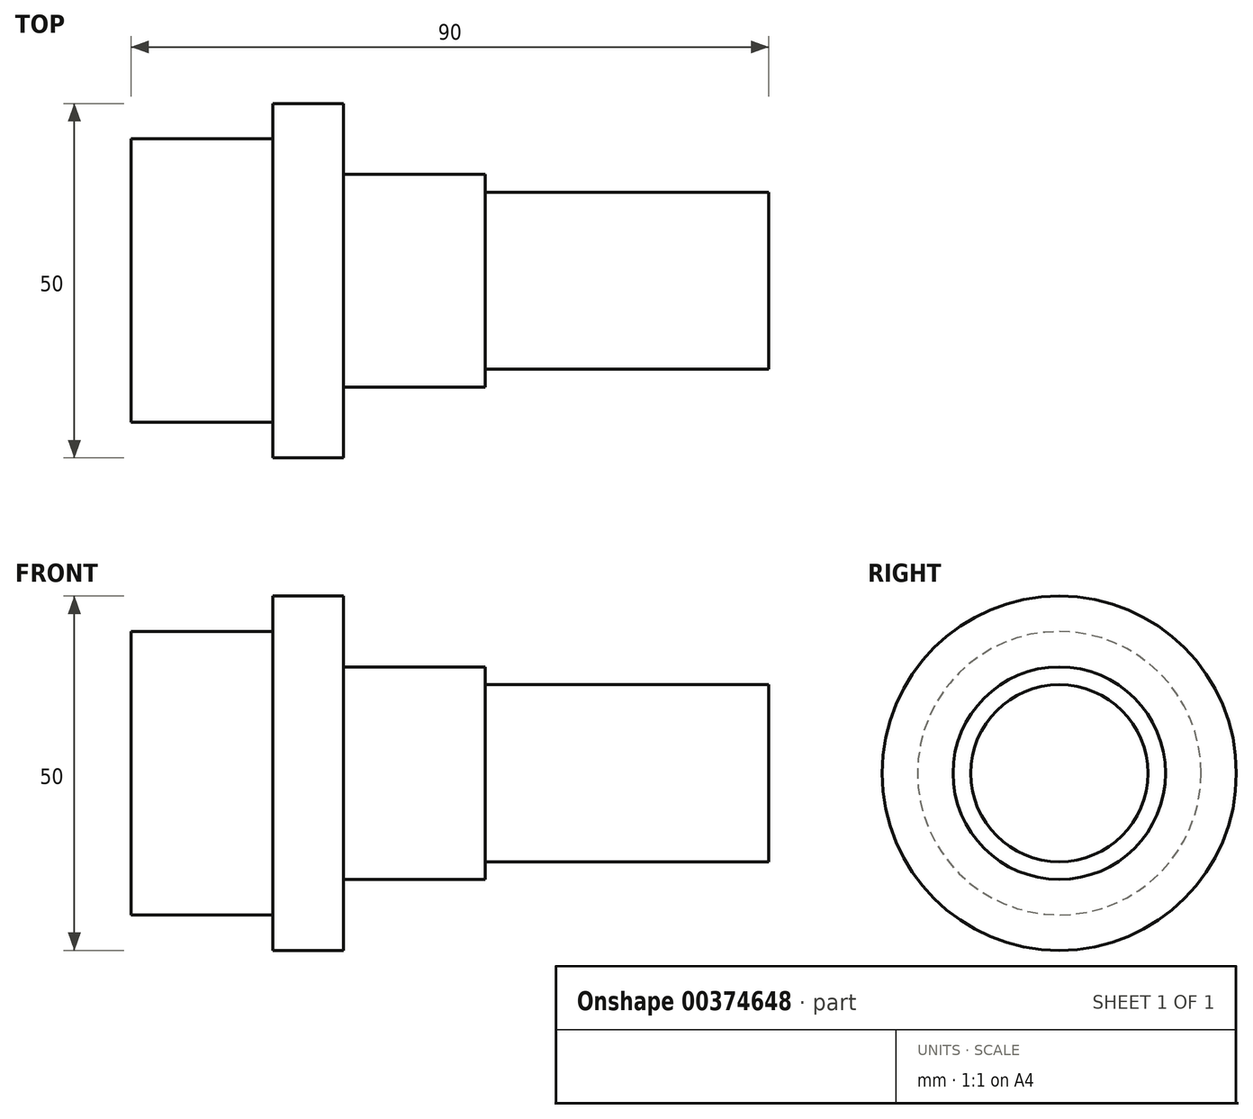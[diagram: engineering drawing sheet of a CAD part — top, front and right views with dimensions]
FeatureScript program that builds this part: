
annotation { "Feature Type Name" : "Feature", "Feature Type Description" : "" }
export const myFeature = defineFeature(function(context is Context, id is Id, definition is map)
    precondition{}
    {
        {
            var Q0;
            Q0=qCreatedBy(makeId("Front.planeOp"),FACE);
            var sketch = newSketch(context, id + "F0", { "sketchPlane" : qUnion([Q0])});
            skLineSegment(sketch, "E0", {"start": v(0, 0) * mm, "end": v(0, 20) * mm});
            skLineSegment(sketch, "E1", {"start": v(0, 20) * mm, "end": v(20, 20) * mm});
            skLineSegment(sketch, "E2", {"start": v(20, 20) * mm, "end": v(20, 25) * mm});
            skLineSegment(sketch, "E3", {"start": v(20, 25) * mm, "end": v(30, 25) * mm});
            skLineSegment(sketch, "E4", {"start": v(30, 25) * mm, "end": v(30, 15) * mm});
            skLineSegment(sketch, "E5", {"start": v(30, 15) * mm, "end": v(50, 15) * mm});
            skLineSegment(sketch, "E6", {"start": v(50, 15) * mm, "end": v(50, 12.5) * mm});
            skLineSegment(sketch, "E7", {"start": v(50, 12.5) * mm, "end": v(90, 12.5) * mm});
            skLineSegment(sketch, "E8", {"start": v(90, 12.5) * mm, "end": v(90, 0) * mm});
            skLineSegment(sketch, "E9", {"start": v(90, 0) * mm, "end": v(0, 0) * mm});
            skSolve(sketch);
        }
        {
            var Q0;
            Q0 = qSketchRegion(id + "F0", true);
            var Q1;
            Q1=sQuery(id+"F0.wireOp",EDGE,"E9");
            revolve(context, id + "F1", {"entities" : qUnion([Q0]), "axis" : qUnion([Q1]), "revolveType" : RevolveType.FULL});
        }
    });
